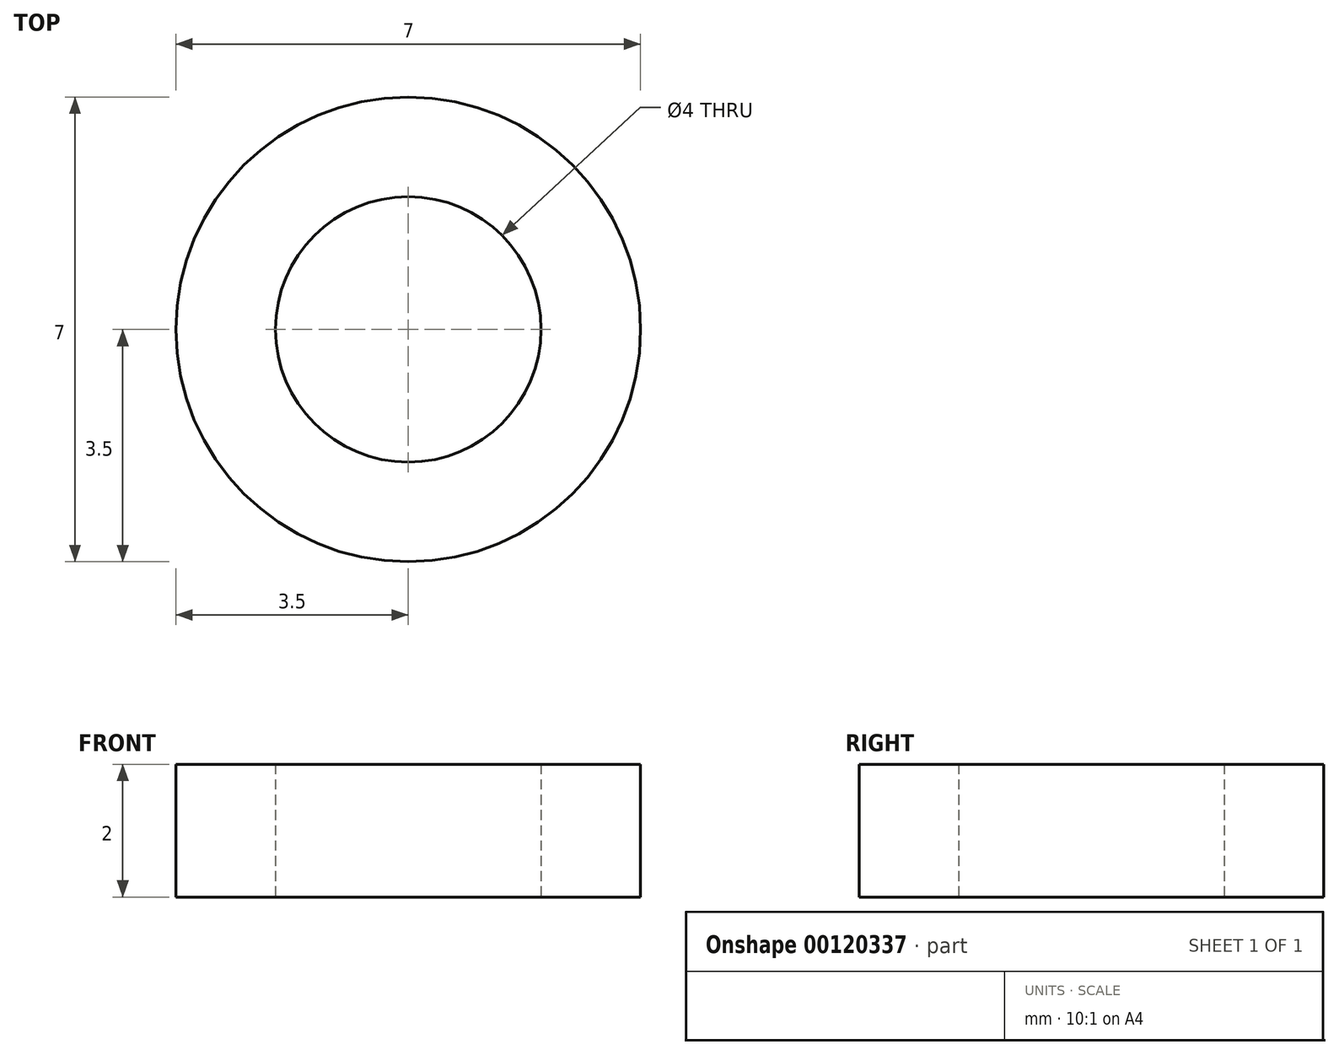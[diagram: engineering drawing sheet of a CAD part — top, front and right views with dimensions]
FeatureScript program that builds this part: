
annotation { "Feature Type Name" : "Feature", "Feature Type Description" : "" }
export const myFeature = defineFeature(function(context is Context, id is Id, definition is map)
    precondition{}
    {
        {
            var Q0;
            Q0=qCreatedBy(makeId("Top.planeOp"),FACE);
            var sketch = newSketch(context, id + "F0", { "sketchPlane" : qUnion([Q0])});
            skCircle(sketch, "E0", {"center": v(0, 0) * mm, "radius": 2 * mm});
            skCircle(sketch, "E1", {"center": v(0, 0) * mm, "radius": 3.5 * mm});
            skSolve(sketch);
        }
        {
            var Q0;
            Q0 = qSketchRegion(id + "F0", true);
            extrude(context, id + "F1", {"entities" : qUnion([Q0]), "depth" : 2 * mm});
        }
    });
